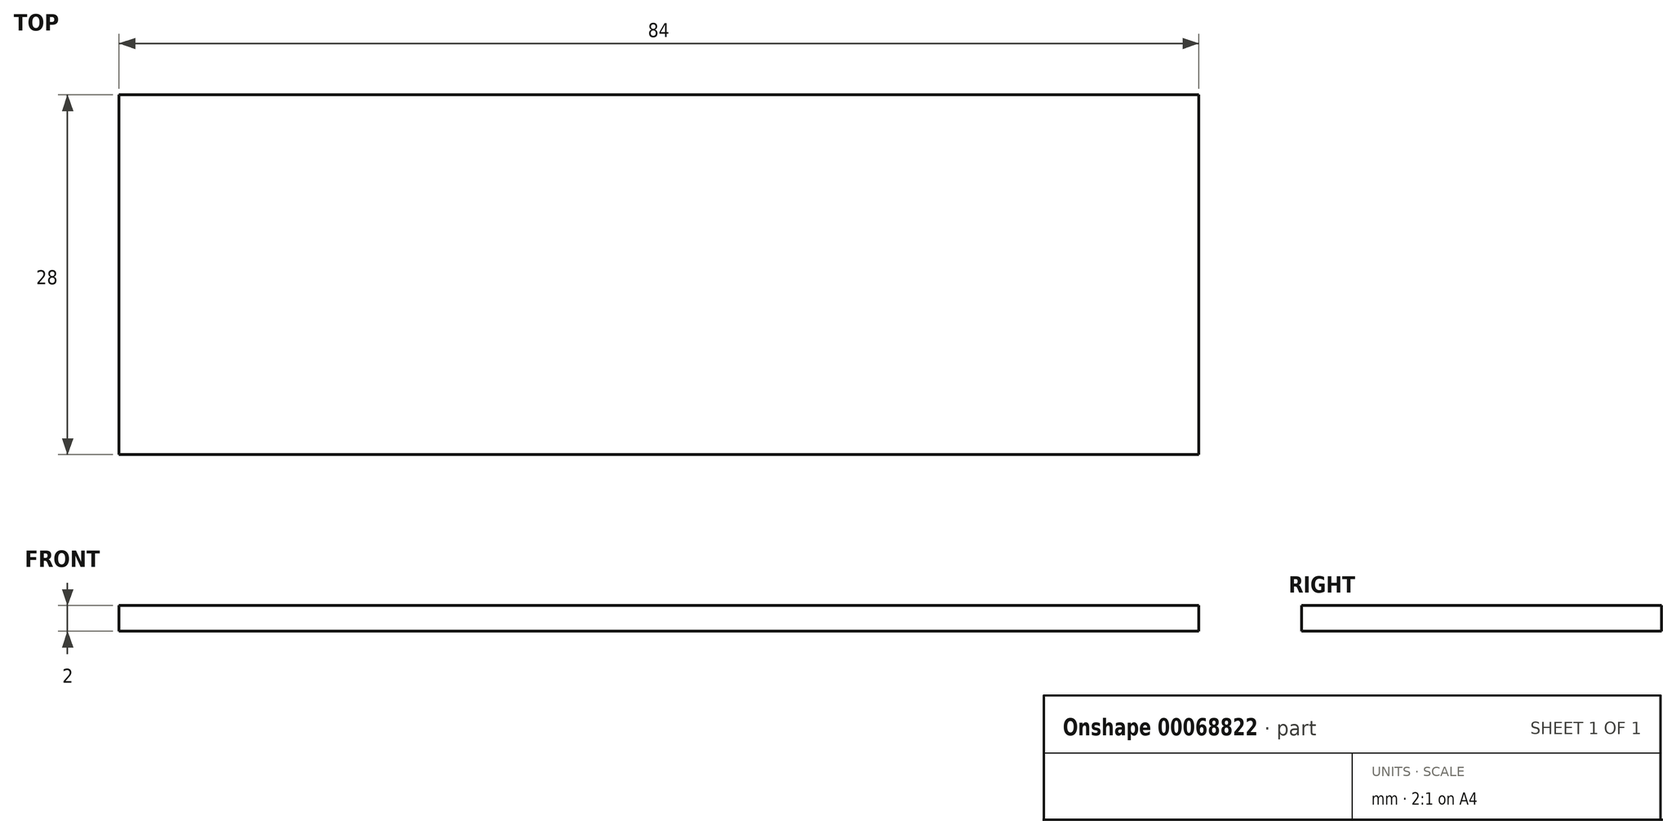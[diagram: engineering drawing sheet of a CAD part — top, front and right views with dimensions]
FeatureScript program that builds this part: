
annotation { "Feature Type Name" : "Feature", "Feature Type Description" : "" }
export const myFeature = defineFeature(function(context is Context, id is Id, definition is map)
    precondition{}
    {
        {
            var Q0;
            Q0=qCreatedBy(makeId("Top.planeOp"),FACE);
            var sketch = newSketch(context, id + "F0", { "sketchPlane" : qUnion([Q0])});
            skLineSegment(sketch, "E0.bottom", {"start": v(0, 0) * mm, "end": v(84, 0) * mm});
            skLineSegment(sketch, "E0.top", {"start": v(0, -28) * mm, "end": v(84, -28) * mm});
            skLineSegment(sketch, "E0.left", {"start": v(0, 0) * mm, "end": v(0, -28) * mm});
            skLineSegment(sketch, "E0.right", {"start": v(84, 0) * mm, "end": v(84, -28) * mm});
            skSolve(sketch);
        }
        {
            var Q0;
            Q0 = qSketchRegion(id + "F0", true);
            extrude(context, id + "F1", {"entities" : qUnion([Q0]), "depth" : 2 * mm});
        }
    });
